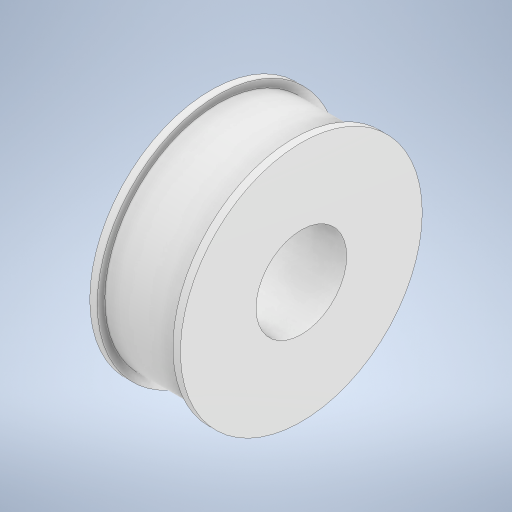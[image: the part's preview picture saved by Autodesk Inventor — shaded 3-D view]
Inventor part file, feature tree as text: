
AUTODESK INVENTOR PART (.ipt)
format: ipt  version: 2023 (Build 270158000, 158)  size: 253,952 bytes
history: native  units: mm
features: extrude x4, sketch x4, other x1
ambient origin geometry x8: Origin, YZ Plane, XZ Plane, XY Plane, X Axis, Y Axis, Z Axis, Center Point
bodies: Body1 (feature_tree)
feature tree (9):
  other  "ソリッド1"
  extrude  "押し出し1"  Depth=30.0mm
  extrude  "押し出し2"  Depth=10.0mm TaperAngle=0.0deg
  extrude  "押し出し3"  Depth=32.0mm
  extrude  "押し出し4"  Depth=1.0mm TaperAngle=0.0deg
  sketch  "スケッチ1"
  sketch  "スケッチ2"
  sketch  "スケッチ3"
  sketch  "スケッチ4"
